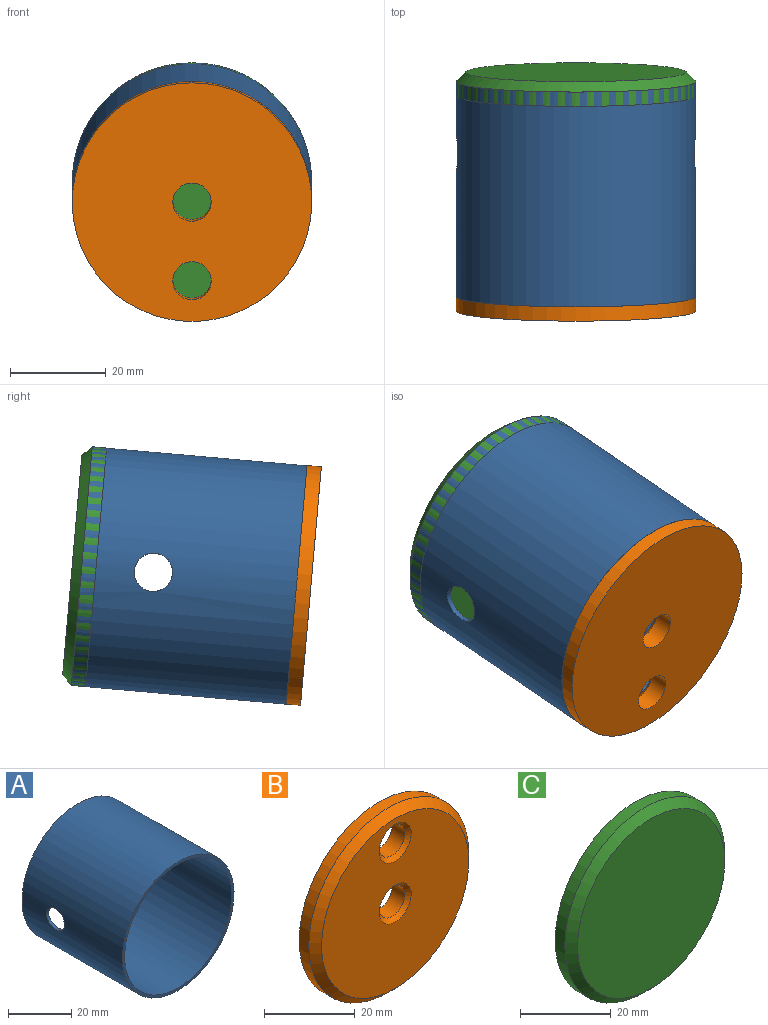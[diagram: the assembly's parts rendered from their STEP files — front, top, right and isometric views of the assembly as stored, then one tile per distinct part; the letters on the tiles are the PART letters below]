
ASSEMBLY  parts=3 mates=1
PART A: 6 faces, bbox 50x45x50 mm
  f0: cylinder r=24mm len=48mm, axis (0,-1,0), area 6685.5mm2, adj f1,f2,f4,f5
  f1: plane 50x50mm, normal (0,1,0), area 153.9mm2, adj f0,f3
  f2: plane 50x50mm, normal (0,-1,0), area 153.9mm2, adj f0,f3
  f3: cylinder r=25mm len=50mm, axis (0,-1,0), area 6967.2mm2, adj f1,f2,f4,f5
  f4: cylinder r=4mm len=8mm, axis (1,0,0), area 25.3mm2, adj f0,f3
  f5: cylinder r=4mm len=8mm, axis (1,0,0), area 25.3mm2, adj f0,f3
PART B: 8 faces, bbox 50x5x50 mm
  f0: cylinder r=4mm len=8mm, axis (0,-1,0), area 100.5mm2, adj f1,f7
  f1: plane 50x50mm, normal (0,1,0), area 1863mm2, adj f0,f3,f5
  f2: plane 46x46mm, normal (0,-1,0), area 1504.8mm2, adj f4,f6,f7
  f3: cylinder r=25mm len=50mm, axis (0,-1,0), area 471.2mm2, adj f1,f4
  f4: cone r=23mm half-angle=45deg, axis (0,1,0), area 426.5mm2, adj f2,f3
  f5: cylinder r=4mm len=8mm, axis (0,-1,0), area 100.5mm2, adj f1,f6
  f6: cone r=4mm half-angle=45deg, axis (0,-1,0), area 40mm2, adj f2,f5
  f7: cone r=4mm half-angle=45deg, axis (0,-1,0), area 40mm2, adj f0,f2
PART C: 4 faces, bbox 50x5x50 mm
  f0: plane 50x50mm, normal (0,1,0), area 1963.5mm2, adj f2
  f1: plane 46x46mm, normal (0,-1,0), area 1661.9mm2, adj f3
  f2: cylinder r=25mm len=50mm, axis (0,-1,0), area 471.2mm2, adj f0,f3
  f3: cone r=23mm half-angle=45deg, axis (0,1,0), area 426.5mm2, adj f1,f2
PLACE A rot(axis=(1,0,0),5deg) t=(30.89,27.37,26.23)mm
PLACE B rot(axis=(-1,0,0),175deg) t=(30.89,-20.45,22.05)mm
PLACE C rot(axis=(-1,0,0),175deg) t=(30.89,24.38,25.97)mm
MATE fastened B.f4 <-> A.f0  axis (0,1,0.09) through (30.89,-17.46,22.31)mm
